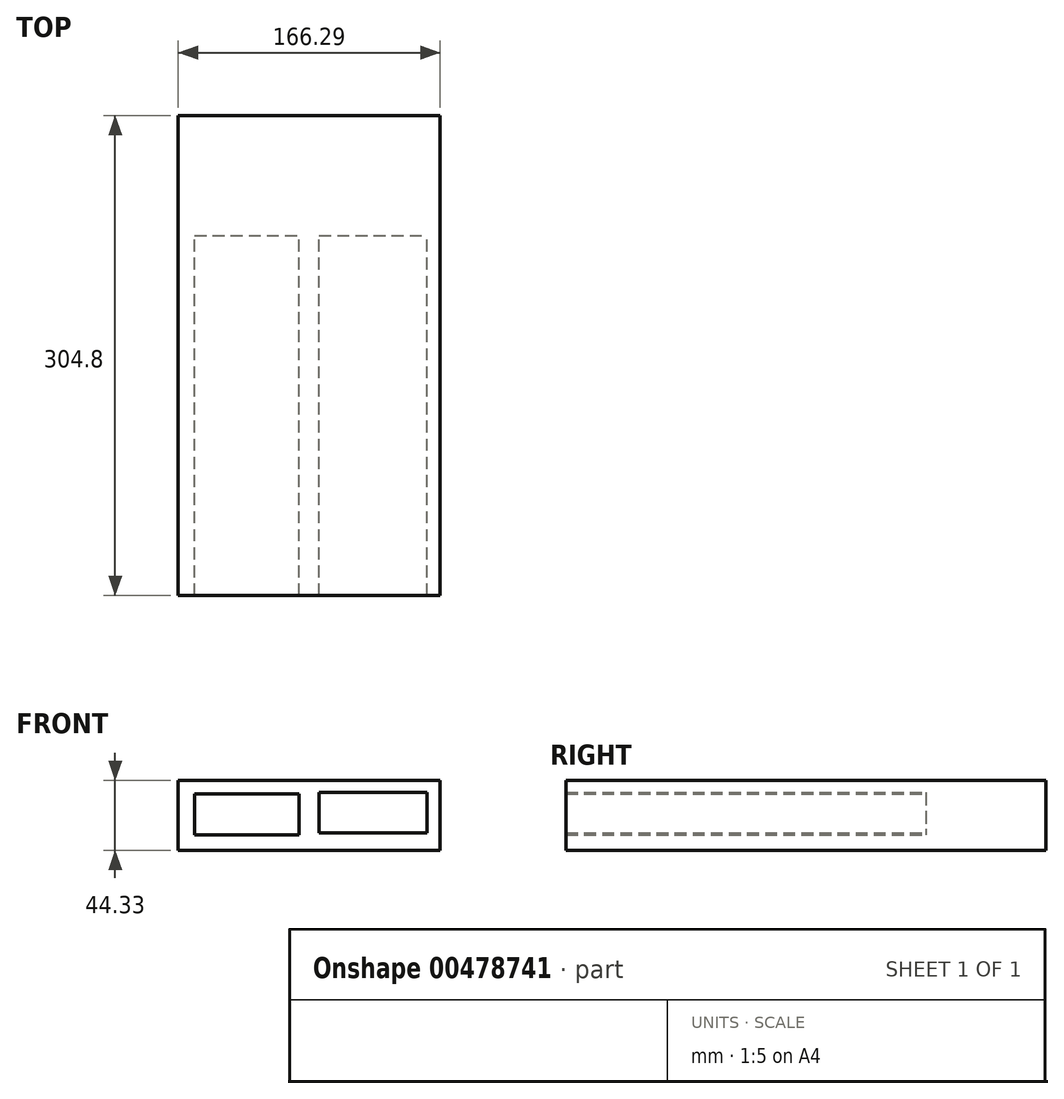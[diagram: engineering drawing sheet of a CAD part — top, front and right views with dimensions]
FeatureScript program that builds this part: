
annotation { "Feature Type Name" : "Feature", "Feature Type Description" : "" }
export const myFeature = defineFeature(function(context is Context, id is Id, definition is map)
    precondition{}
    {
        {
            var Q0;
            Q0=qCreatedBy(makeId("Front.planeOp"),FACE);
            var sketch = newSketch(context, id + "F0", { "sketchPlane" : qUnion([Q0])});
            skLineSegment(sketch, "E0.bottom", {"start": v(-54.8, 44.33) * mm, "end": v(111.49, 44.33) * mm});
            skLineSegment(sketch, "E0.top", {"start": v(-54.8, 0) * mm, "end": v(111.49, 0) * mm});
            skLineSegment(sketch, "E0.left", {"start": v(-54.8, 44.33) * mm, "end": v(-54.8, 0) * mm});
            skLineSegment(sketch, "E0.right", {"start": v(111.49, 44.33) * mm, "end": v(111.49, 0) * mm});
            skSolve(sketch);
        }
        {
            var Q0;
            Q0=makeQuery(id+"F0.imprint","IMPRINT",FACE,{"disambiguationData":[TD([[makeQuery(id+"F0.imprint","IMPRINT",EDGE,{"derivedFrom":sQuery(id+"F0.wireOp",EDGE,"E0.bottom")}),-1.0]])]});
            var sketch = newSketch(context, id + "F1", { "sketchPlane" : qUnion([Q0])});
            skLineSegment(sketch, "E1.bottom", {"start": v(-44.46, 35.86) * mm, "end": v(22.04, 35.86) * mm});
            skLineSegment(sketch, "E1.top", {"start": v(-44.46, 9.86) * mm, "end": v(22.04, 9.86) * mm});
            skLineSegment(sketch, "E1.left", {"start": v(-44.46, 35.86) * mm, "end": v(-44.46, 9.86) * mm});
            skLineSegment(sketch, "E1.right", {"start": v(22.04, 35.86) * mm, "end": v(22.04, 9.86) * mm});
            skSolve(sketch);
        }
        {
            var Q0;
            Q0=makeQuery(id+"F0.imprint","IMPRINT",FACE,{"disambiguationData":[TD([[makeQuery(id+"F0.imprint","IMPRINT",EDGE,{"derivedFrom":sQuery(id+"F0.wireOp",EDGE,"E0.bottom")}),-1.0]])]});
            var sketch = newSketch(context, id + "F2", { "sketchPlane" : qUnion([Q0])});
            skLineSegment(sketch, "E2.bottom", {"start": v(34.75, 36.63) * mm, "end": v(103.31, 36.63) * mm});
            skLineSegment(sketch, "E2.top", {"start": v(34.75, 11.1) * mm, "end": v(103.31, 11.1) * mm});
            skLineSegment(sketch, "E2.left", {"start": v(34.75, 36.63) * mm, "end": v(34.75, 11.1) * mm});
            skLineSegment(sketch, "E2.right", {"start": v(103.31, 36.63) * mm, "end": v(103.31, 11.1) * mm});
            skSolve(sketch);
        }
        {
            var Q0;
            Q0=sQuery(id+"F0.wireOp",EDGE,"E0.left");
            var Q1;
            Q1=sQuery(id+"F0.wireOp",EDGE,"E0.bottom");
            var Q2;
            Q2=sQuery(id+"F0.wireOp",EDGE,"E0.top");
            var Q3;
            Q3=sQuery(id+"F0.wireOp",EDGE,"E0.right");
            extrude(context, id + "F3", {"bodyType" : ToolBodyType.SURFACE, "surfaceEntities" : qUnion([Q0, Q1, Q2, Q3]), "depth" : -304.8 * mm});
        }
        {
            var Q0;
            Q0=sQuery(id+"F2.wireOp",EDGE,"E2.bottom");
            var Q1;
            Q1=sQuery(id+"F2.wireOp",EDGE,"E2.top");
            var Q2;
            Q2=sQuery(id+"F2.wireOp",EDGE,"E2.left");
            var Q3;
            Q3=sQuery(id+"F2.wireOp",EDGE,"E2.right");
            extrude(context, id + "F4", {"bodyType" : ToolBodyType.SURFACE, "surfaceEntities" : qUnion([Q0, Q1, Q2, Q3]), "depth" : -228.6 * mm});
        }
        {
            var Q0;
            Q0=sQuery(id+"F1.wireOp",EDGE,"E1.right");
            var Q1;
            Q1=sQuery(id+"F1.wireOp",EDGE,"E1.bottom");
            var Q2;
            Q2=sQuery(id+"F1.wireOp",EDGE,"E1.top");
            var Q3;
            Q3=sQuery(id+"F1.wireOp",EDGE,"E1.left");
            extrude(context, id + "F5", {"bodyType" : ToolBodyType.SURFACE, "surfaceEntities" : qUnion([Q0, Q1, Q2, Q3]), "depth" : -228.6 * mm});
        }
    });
